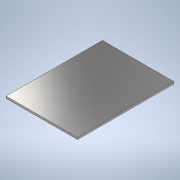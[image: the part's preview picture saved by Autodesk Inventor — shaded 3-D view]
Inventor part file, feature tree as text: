
AUTODESK INVENTOR PART (.ipt)
format: ipt  version: 2020 (Build 240168000, 168)  size: 94,720 bytes
history: native  units: in
note: dims shown in document units (in); Inventor stores cm internally (conversion verified against a paired STEP export)
features: extrude x1, sketch x1
ambient origin geometry x8: Origin, YZ Plane, XZ Plane, XY Plane, X Axis, Y Axis, Z Axis, Center Point
bodies: Solid1 (feature_tree)
feature tree (2):
  extrude  "Extrusion1"  [1 undecoded]
  sketch  "Sketch1"  dims[d0=0.0787in d1=0.0in]
note: 1 required parameter value undecoded (feature->parameter linkage not recoverable at this tier; creation-order binding heuristic only, values carry confidence <= 0.55)
